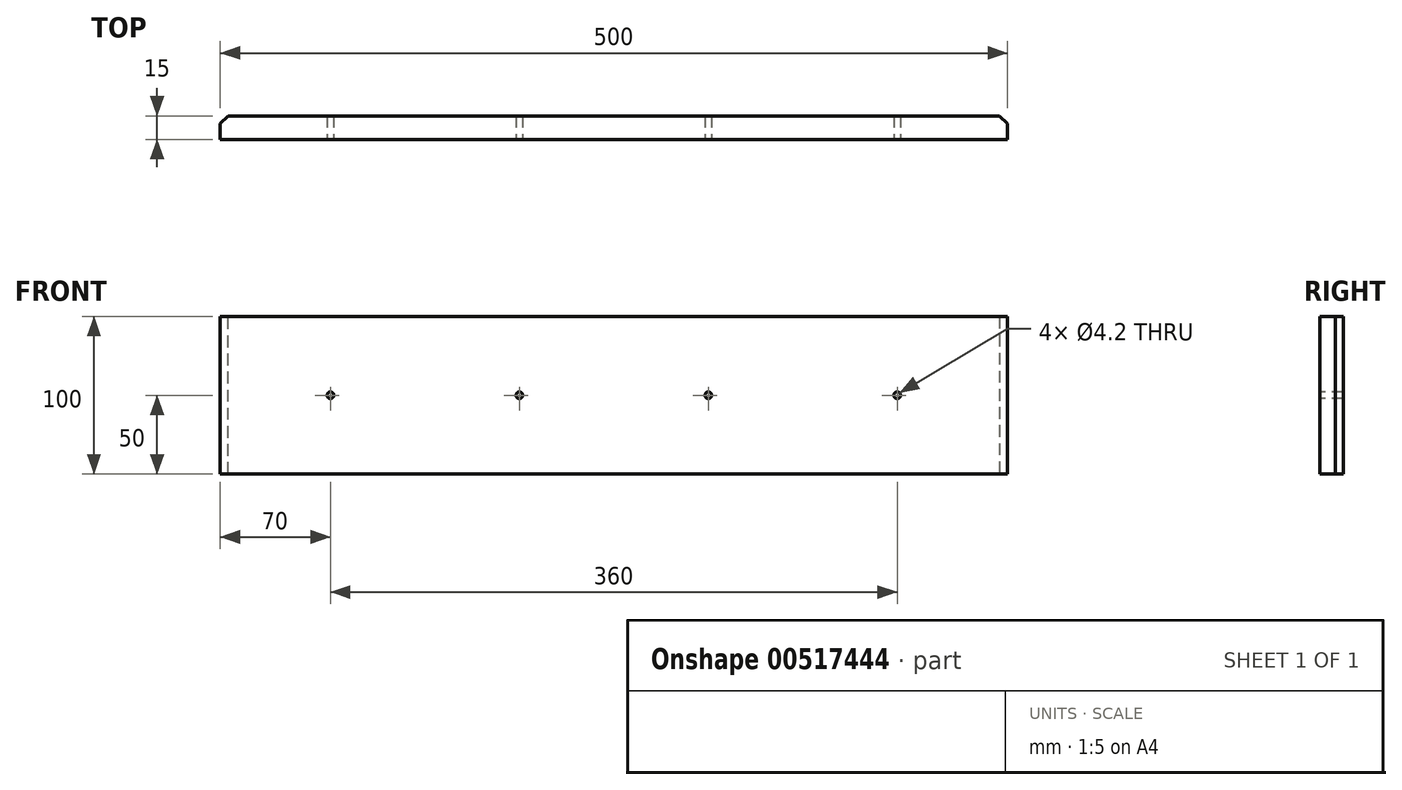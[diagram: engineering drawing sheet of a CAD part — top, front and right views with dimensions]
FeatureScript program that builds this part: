
annotation { "Feature Type Name" : "Feature", "Feature Type Description" : "" }
export const myFeature = defineFeature(function(context is Context, id is Id, definition is map)
    precondition{}
    {
        {
            var Q0;
            Q0=qCreatedBy(makeId("Front.planeOp"),FACE);
            var sketch = newSketch(context, id + "F0", { "sketchPlane" : qUnion([Q0])});
            skLineSegment(sketch, "E0.bottom", {"start": v(250, -50) * mm, "end": v(-250, -50) * mm});
            skLineSegment(sketch, "E0.top", {"start": v(250, 50) * mm, "end": v(-250, 50) * mm});
            skLineSegment(sketch, "E0.left", {"start": v(250, -50) * mm, "end": v(250, 50) * mm});
            skLineSegment(sketch, "E0.right", {"start": v(-250, -50) * mm, "end": v(-250, 50) * mm});
            skPoint(sketch, "E0.middle", {"position": v(0, 0) * mm});
            skSolve(sketch);
        }
        {
            var Q0;
            Q0=makeQuery(id+"F0.imprint","IMPRINT",FACE,{"disambiguationData":[TD([[makeQuery(id+"F0.imprint","IMPRINT",EDGE,{"derivedFrom":sQuery(id+"F0.wireOp",EDGE,"E0.bottom")}),-1.0]])]});
            extrude(context, id + "F1", {"entities" : qUnion([Q0]), "depth" : 15 * mm, "offsetDistance" : 25 * mm});
        }
        {
            var Q0;
            Q0=makeQuery(id+"F1.opExtrude","CAP_FACE",FACE,{"disambiguationData":[OSD([sQuery(id+"F0.wireOp",EDGE,"E0.bottom"),sQuery(id+"F0.wireOp",EDGE,"E0.top"),sQuery(id+"F0.wireOp",EDGE,"E0.left"),sQuery(id+"F0.wireOp",EDGE,"E0.right")])],"isStart":false});
            var sketch = newSketch(context, id + "F2", { "sketchPlane" : qUnion([Q0])});
            skLineSegment(sketch, "E1", {"start": v(-60, 0) * mm, "end": v(60, 0) * mm});
            skLineSegment(sketch, "E2", {"start": v(60, 0) * mm, "end": v(180, 0) * mm});
            skLineSegment(sketch, "E3", {"start": v(-60, 0) * mm, "end": v(-180, 0) * mm});
            skSolve(sketch);
        }
        {
            var Q0;
            Q0=sQuery(id+"F2.wireOp",VERTEX,"E3.end");
            var Q1;
            Q1=sQuery(id+"F2.wireOp",VERTEX,"E3.start");
            var Q2;
            Q2=sQuery(id+"F2.wireOp",VERTEX,"E2.start");
            var Q3;
            Q3=sQuery(id+"F2.wireOp",VERTEX,"E2.end");
            var Q4;
            Q4=makeQuery(id+"F1.opExtrude","SWEPT_BODY",BODY,{"disambiguationData":[OSD([sQuery(id+"F0.wireOp",EDGE,"E0.bottom"),sQuery(id+"F0.wireOp",EDGE,"E0.top"),sQuery(id+"F0.wireOp",EDGE,"E0.left"),sQuery(id+"F0.wireOp",EDGE,"E0.right")])]});
            hole(context, id + "F3", {"style" : HoleStyle.SIMPLE, "endStyle" : HoleEndStyle.THROUGH, "standardTappedOrClearance" : lookupTablePath({ "standard" : "ISO", "engagement" : "75%", "pitch" : "0.8 mm", "size" : "M5", "type" : "Tapped" }), "standardBlindInLast" : lookupTablePath({ "standard" : "ISO", "engagement" : "75%", "pitch" : "0.8 mm", "size" : "M5", "type" : "Tapped" }), "holeDiameter" : 4.2 * mm, "showTappedDepth" : true, "isTappedThrough" : true, "tappedDepth" : 12 * mm, "tapClearance" : 3, "locations" : qUnion([Q0, Q1, Q2, Q3]), "scope" : qUnion([Q4]), "majorDiameter" : 5 * mm});
        }
        {
            var Q0;
            Q0=makeQuery(id+"F1.opExtrude","CAP_EDGE",EDGE,{"disambiguationData":[OSD([sQuery(id+"F0.wireOp",EDGE,"E0.right")])],"isStart":true});
            var Q1;
            Q1=makeQuery(id+"F1.opExtrude","CAP_EDGE",EDGE,{"disambiguationData":[OSD([sQuery(id+"F0.wireOp",EDGE,"E0.left")])],"isStart":true});
            chamfer(context, id + "F4", {"entities" : qUnion([Q0, Q1]), "width" : 5 * mm, "tangentPropagation" : true});
        }
    });
